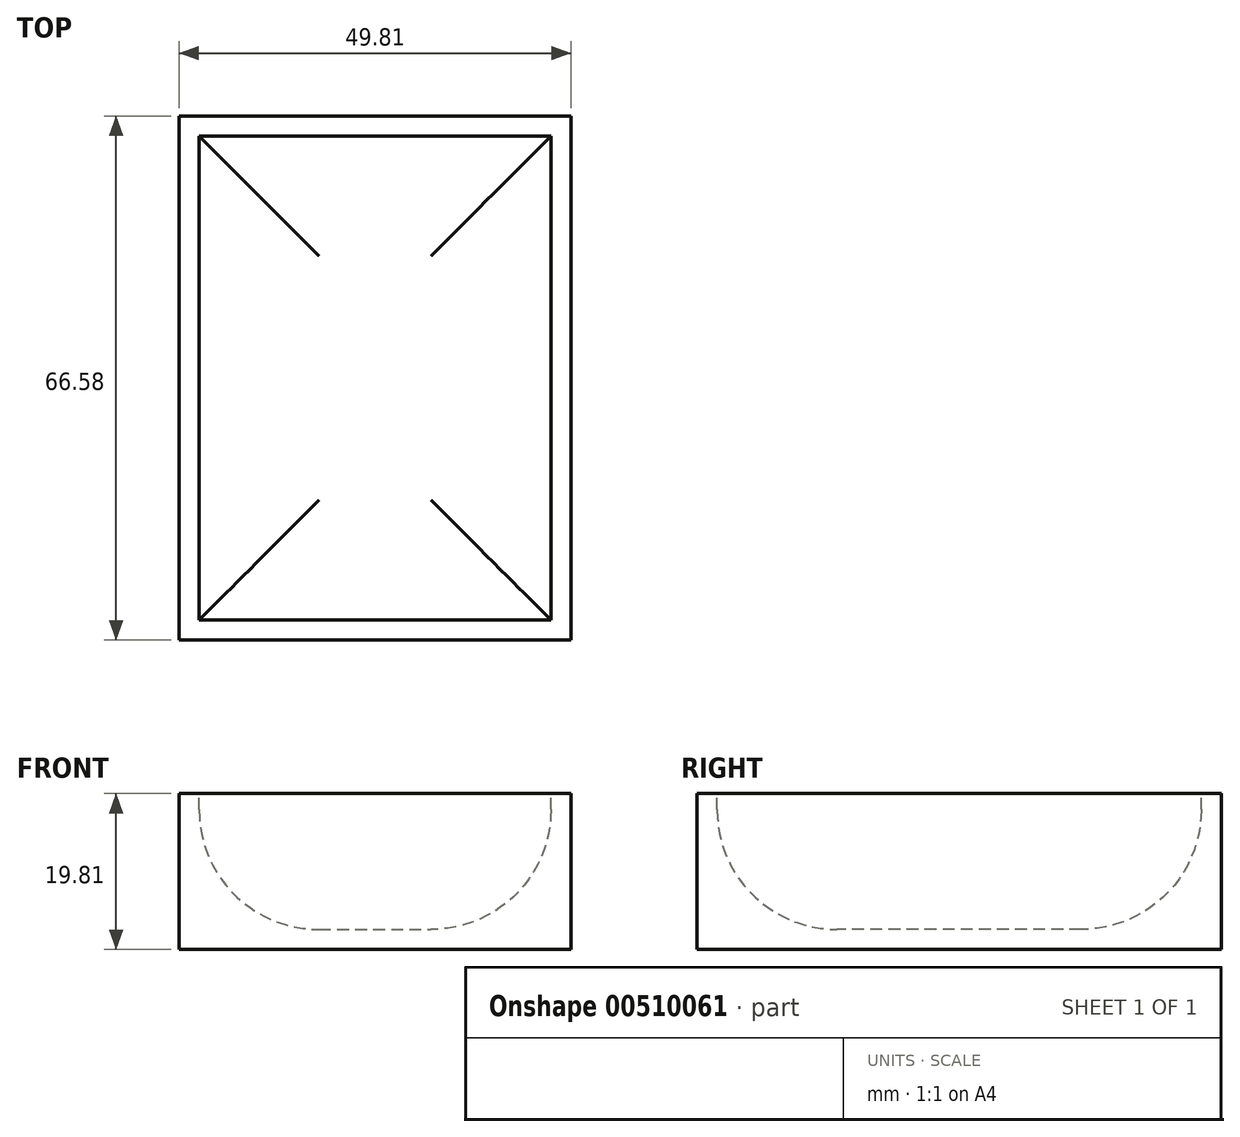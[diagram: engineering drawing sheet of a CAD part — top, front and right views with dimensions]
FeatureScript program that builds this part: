
annotation { "Feature Type Name" : "Feature", "Feature Type Description" : "" }
export const myFeature = defineFeature(function(context is Context, id is Id, definition is map)
    precondition{}
    {
        {
            var Q0;
            Q0=qCreatedBy(makeId("Top.planeOp"),FACE);
            var sketch = newSketch(context, id + "F0", { "sketchPlane" : qUnion([Q0])});
            skLineSegment(sketch, "E0.bottom", {"start": v(-30.71, 37.42) * mm, "end": v(19.1, 37.42) * mm});
            skLineSegment(sketch, "E0.top", {"start": v(-30.71, -29.16) * mm, "end": v(19.1, -29.16) * mm});
            skLineSegment(sketch, "E0.left", {"start": v(-30.71, 37.42) * mm, "end": v(-30.71, -29.16) * mm});
            skLineSegment(sketch, "E0.right", {"start": v(19.1, 37.42) * mm, "end": v(19.1, -29.16) * mm});
            skSolve(sketch);
        }
        {
            var Q0;
            Q0=makeQuery(id+"F0.imprint","IMPRINT",FACE,{"disambiguationData":[TD([[makeQuery(id+"F0.imprint","IMPRINT",EDGE,{"derivedFrom":sQuery(id+"F0.wireOp",EDGE,"E0.bottom")}),-1.0]])]});
            extrude(context, id + "F1", {"entities" : qUnion([Q0]), "depth" : -19.8 * mm});
        }
        {
            var Q0;
            Q0=makeQuery(id+"F1.opExtrude","CAP_FACE",FACE,{"disambiguationData":[OSD([sQuery(id+"F0.wireOp",EDGE,"E0.bottom"),sQuery(id+"F0.wireOp",EDGE,"E0.top"),sQuery(id+"F0.wireOp",EDGE,"E0.left"),sQuery(id+"F0.wireOp",EDGE,"E0.right")])],"isStart":true});
            shell(context, id + "F2", {"entities" : qUnion([Q0]), "thickness" : 2.54 * mm});
        }
        {
            var Q0;
            {var subQ0=sQuery(id+"F0.wireOp",EDGE,"E0.right");Q0=makeQuery(id+"F2.opShell","OFFSET_EDGE",EDGE,{"disambiguationData":[OSD([subQ0]),TDD([makeQuery(id+"F1.opExtrude","CAP_EDGE",EDGE,{"disambiguationData":[OSD([subQ0])],"isStart":false})])]});}
            var Q1;
            {var subQ0=sQuery(id+"F0.wireOp",EDGE,"E0.top");Q1=makeQuery(id+"F2.opShell","OFFSET_EDGE",EDGE,{"disambiguationData":[OSD([subQ0]),TDD([makeQuery(id+"F1.opExtrude","CAP_EDGE",EDGE,{"disambiguationData":[OSD([subQ0])],"isStart":false})])]});}
            var Q2;
            {var subQ0=sQuery(id+"F0.wireOp",EDGE,"E0.bottom");Q2=makeQuery(id+"F2.opShell","OFFSET_EDGE",EDGE,{"disambiguationData":[OSD([subQ0]),TDD([makeQuery(id+"F1.opExtrude","CAP_EDGE",EDGE,{"disambiguationData":[OSD([subQ0])],"isStart":false})])]});}
            var Q3;
            {var subQ0=sQuery(id+"F0.wireOp",EDGE,"E0.left");Q3=makeQuery(id+"F2.opShell","OFFSET_EDGE",EDGE,{"disambiguationData":[OSD([subQ0]),TDD([makeQuery(id+"F1.opExtrude","CAP_EDGE",EDGE,{"disambiguationData":[OSD([subQ0])],"isStart":false})])]});}
            fillet(context, id + "F3", {"entities" : qUnion([Q0, Q1, Q2, Q3]), "radius" : 15.24 * mm, "tangentPropagation" : true, "allowEdgeOverflow" : false});
        }
    });
